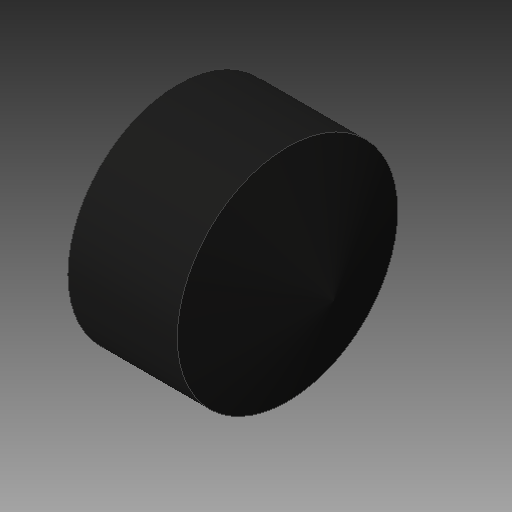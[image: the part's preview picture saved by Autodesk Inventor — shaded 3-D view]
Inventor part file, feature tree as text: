
AUTODESK INVENTOR PART (.ipt)
format: ipt  version: 2019 (Build 230136000, 136)  size: 135,168 bytes
history: native  units: in
note: dims shown in document units (in); Inventor stores cm internally (conversion verified against a paired STEP export)
features: revolve x1, sketch x1
ambient origin geometry x8: Origin, YZ Plane, XZ Plane, XY Plane, X Axis, Y Axis, Z Axis, Center Point
bodies: Solid1 (feature_tree)
feature tree (2):
  revolve  "Revolution1"  [1 undecoded]
  sketch  "Sketch1"  dims[d0=0.2205in d1=0.5512in d2=0.6976in d3=0.6268in d4=0.3543in d5=0.1575in d6=0.122in d7=0.2717in d8=0.8921in d9=90.0deg]
note: 1 required parameter value undecoded (feature->parameter linkage not recoverable at this tier; creation-order binding heuristic only, values carry confidence <= 0.55)
